# Revit family: PRD_AR_MxrTps_ThermostaticSingle-leverWall-mountedMixer_F5LT1004-F5LT1006
name_source: partatom
category: Plumbing Fixtures
units: mm (PartAtom-declared; Revit-internal decimal feet)

## family parameters
Cut with Voids When Loaded = Yes
Host = Face
OmniClass Number = 23.45.55.17
OmniClass Title = Mixing Faucets
Part Type = Normal
Room Calculation Point = No
Round Connector Dimension = Use Diameter
Shared = No

## types (3) — shared parameters
AccentColour = none
AssetType = Fixed
BasicColour = chrome-look (glossy)
BodyMaterial = PRD_AR_ChromatedBrass_HighPolished
Category = Pr_40_20_87_55, Mixer taps
CloseOffRating = 0.0 Pa
Color = chrome-look (glossy)
Default Elevation = 1219 mm
Depressurised = no
DiameterNominal = 15  [stored 0.0492126 ft]
DurationUnit = year
FaucetFunction = Mixed
FaucetOperation = LeverHandle
FaucetType = Bib
Finish = polished chrome-plated
FunctionalPrinciple = manual
HygieneFlushing = prepared
IfcExportAs = IfcValveType
IfcExportType = FAUCET
InletSize = G 1/2 B
LockingMechanism = Top section, ceramic
Manufacturer = KWC Group AG
ManufacturerName = KWC Group AG
ManufacturerURL = www.kwc.com
Material = Brass
MaterialFitting = brass-look
MinimumFlowPressure = 1 bar
NBSDescription = Taps and water supply fittings for sinks
NBSReference = 45-35-70/345
NominalWidth = 288 mm  [stored 0.944882 ft]
Pop-upWasteSet = no
ProductInformation = http://pim.kwc.com
ProtectiveShutdown = no
Shape = Bib tap
Size = 15
SoundInsulation = no
Spout = rotating, bottom
Status = New
SurfaceFinishCasing = chromed
SurfaceFinishFitting = chromed
SurfaceTreatmentFitting = polished
TailorMade = no
TemperatureLimit = yes
TestPressure = 0.0 Pa
ThermalDisinfection = yes
TypeOfMixing = with thermostat
TypeOfMounting = wall mounting
TypeOfOperation = manual operation
TypeOfTap = bib tap
URL = www.kwc.com
Uniclass2015Code = Pr_40_20_87_55
Uniclass2015Title = Mixer taps
Uniclass2015Version = Products v1.32
ValveMechanism = OTHER
ValveOperation = LEVER
ValvePattern = STRAIGHT_3_PORT
Version = 1
VolumeFlowRate = 0.1 l/s at 3 bar
WarrantyDurationUnit = year
WaterConnection = S-unions
WithBackflowPreventer = yes
WithFilter = yes
WithRosettesOrCoverPlate = yes
WorkingPressure = 0.0 Pa
zero-valued in all types: FlowCoefficient, NominalDepth, NominalHeight

## per-type parameters (varying)
| type | BIMObjectName | Description | Features | Length | ModelNumber | Name | SpoutProjection |
| F5LT1004 | PRD_AR_MixerTaps_ThermostaticSingle-leverWall-mountedMixer_F5LT1004 | F5L-Therm thermostatic single-lever mixer as DN 15 wall-mounted mixer for wall mounting with lockable swivelling spout, for sanitary facilities. Thermostatically-controlled mixer cartridge with expansion element and active scald protection as well as adjustable and turn-proof temperature stop, and ceramic disc technology. With mechanism for optional hygiene unit for automatic hygiene flushing, program-controlled thermal disinfection (additional bypass solenoid-operated flush valve cartridge necessary) and storage of statistical data. For connection to hot and cold water. Scald-protected, safe-touch housing, all-metal construction, high-polished chrome-plated brass. Laminar jet controller with integrated flow rate controller 6.0 l/min. With adjustable and lockable connections with backflow preventers and strainers, fully covered by depth-adjustable screw rosettes. Projection 155 mm. | For connection to hot water and cold water. With integrated flow rate controller 6.0 l/min. Projection 155 mm. | 155 mm  [stored 0.50853 ft] | 2030066483 | F5L-Therm thermostatic single-lever wall-mounted mixer F5LT1004 | 155 mm |
| F5LT1005 | PRD_AR_MixerTaps_ThermostaticSingle-leverWall-mountedMixer_F5LT1005 | F5L-Therm thermostatic single-lever mixer as DN 15 wall-mounted mixer for wall mounting with lockable swivelling spout, for sanitary facilities. Thermostatically-controlled mixer cartridge with expansion element and active scald protection as well as adjustable and turn-proof temperature stop, and ceramic disc technology. With mechanism for optional hygiene unit for automatic hygiene flushing, program-controlled thermal disinfection (additional bypass solenoid-operated flush valve cartridge necessary) and storage of statistical data. For connection to hot and cold water. Scald-protection, safe-touch housing, all-metal construction, high-polished chrome-plated brass. Laminar jet controller with integrated flow rate controller 6.0 l/min. With adjustable and lockable connections with backflow preventers and strainers, fully covered by depth-adjustable screw rosettes. Projection 215 mm. | For connection to hot water and cold water. With integrated flow rate controller 6.0 l/min. Projection 215 mm. | 215 mm | 2030066484 | F5L-Therm thermostatic single-lever wall-mounted mixer F5LT1005 | 215 mm |
| F5LT1006 | PRD_AR_MixerTaps_ThermostaticSingle-leverWall-mountedMixer_F5LT1006 | F5L-Therm thermostatic single-lever mixer as DN 15 wall-mounted mixer for wall mounting with lockable swivelling spout, for sanitary facilities. Thermostatically-controlled mixer cartridge with expansion element and active scald protection as well as adjustable and turn-proof temperature stop, and ceramic disc technology. With mechanism for optional hygiene unit for automatic hygiene flushing, program-controlled thermal disinfection (additional bypass solenoid-operated flush valve cartridge necessary) and storage of statistical data. For connection to hot and cold water. Scald-protection, safe-touch housing, all-metal construction, high-polished chrome-plated brass. Laminar jet controller with integrated flow rate controller 6.0 l/min. With adjustable and lockable connections with backflow preventers and strainers, fully covered by depth-adjustable screw rosettes. Projection 275 mm. | For connection to hot water and cold water. With integrated flow rate controller 6.0 l/min. Projection 275 mm. | 275 mm | 2030066486 | F5L-Therm thermostatic single-lever wall-mounted mixer F5LT1006 | 275 mm |

note: column(s) folded — value = type name in every type: Model, ModelReference

note: [stored X ft] marks values corroborated as IEEE doubles in the binary element streams (Revit-internal decimal feet)

## geometry (parser evidence)
native form markers: Sweep x11
no freeform markers — native parametric forms only
